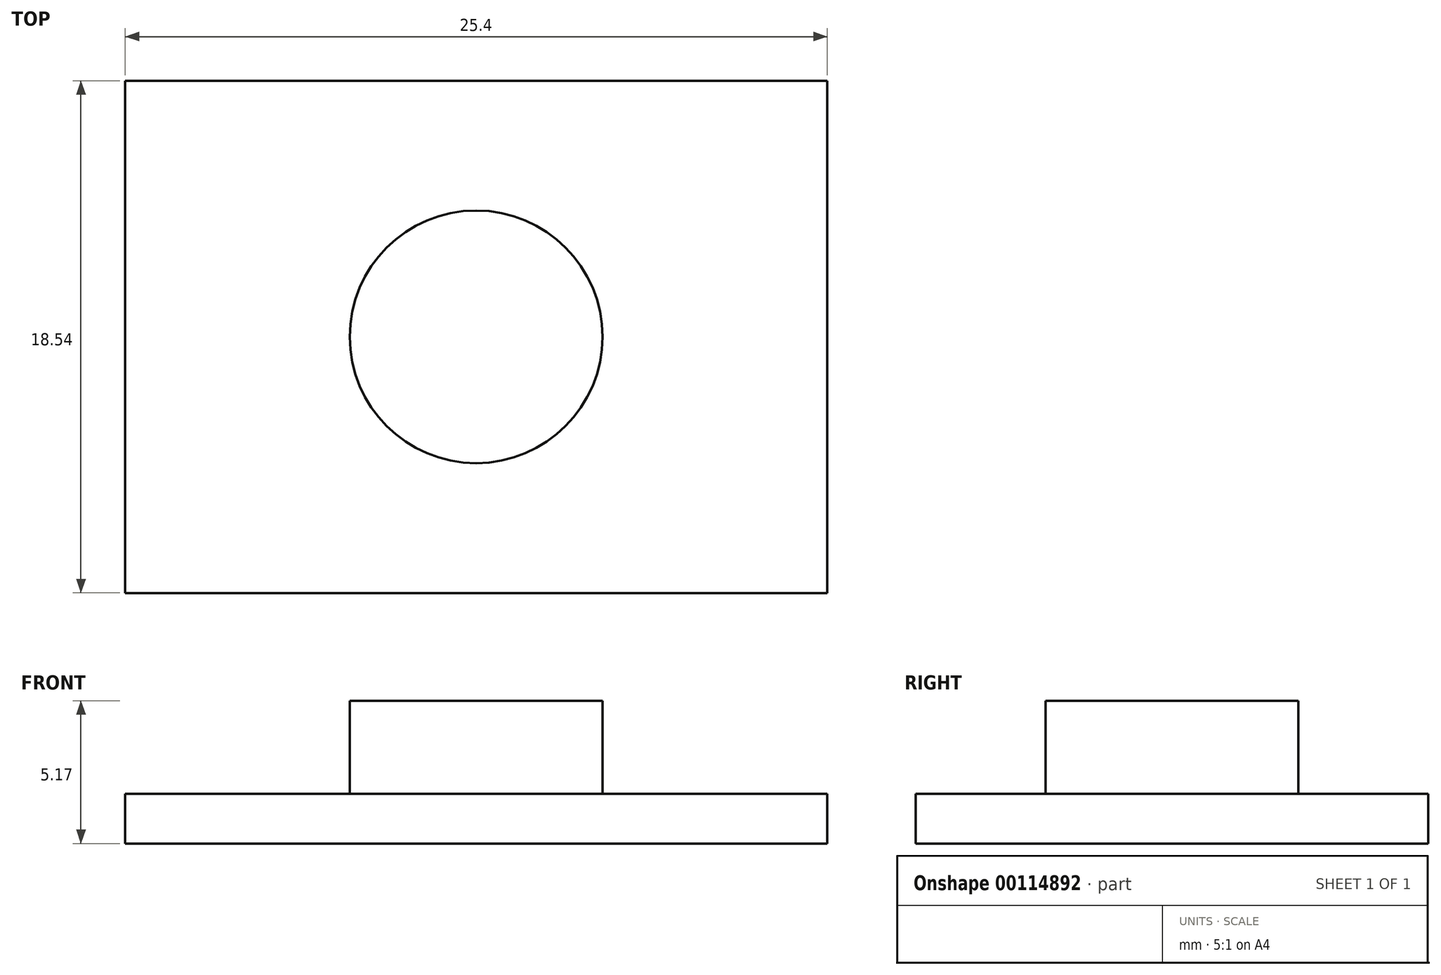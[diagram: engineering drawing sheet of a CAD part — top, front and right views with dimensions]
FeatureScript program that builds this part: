
annotation { "Feature Type Name" : "Feature", "Feature Type Description" : "" }
export const myFeature = defineFeature(function(context is Context, id is Id, definition is map)
    precondition{}
    {
        {
            var Q0;
            Q0=qCreatedBy(makeId("Top.planeOp"),FACE);
            var sketch = newSketch(context, id + "F0", { "sketchPlane" : qUnion([Q0])});
            skLineSegment(sketch, "E0.bottom", {"start": v(-54.14, 26.58) * mm, "end": v(-28.74, 26.58) * mm});
            skLineSegment(sketch, "E0.top", {"start": v(-54.14, 8.04) * mm, "end": v(-28.74, 8.04) * mm});
            skLineSegment(sketch, "E0.left", {"start": v(-54.14, 26.58) * mm, "end": v(-54.14, 8.04) * mm});
            skLineSegment(sketch, "E0.right", {"start": v(-28.74, 26.58) * mm, "end": v(-28.74, 8.04) * mm});
            skSolve(sketch);
        }
        {
            var Q0;
            Q0 = qSketchRegion(id + "F0", true);
            extrude(context, id + "F1", {"entities" : qUnion([Q0]), "depth" : 1.8 * mm});
        }
        {
            var Q0;
            Q0=makeQuery(id+"F1.opExtrude","CAP_FACE",FACE,{"disambiguationData":[OSD([sQuery(id+"F0.wireOp",EDGE,"E0.bottom"),sQuery(id+"F0.wireOp",EDGE,"E0.top"),sQuery(id+"F0.wireOp",EDGE,"E0.left"),sQuery(id+"F0.wireOp",EDGE,"E0.right")])],"isStart":false});
            var sketch = newSketch(context, id + "F2", { "sketchPlane" : qUnion([Q0])});
            skCircle(sketch, "E1", {"center": v(-41.45, 17.31) * mm, "radius": 4.57 * mm});
            skSolve(sketch);
        }
        {
            var Q0;
            Q0 = qSketchRegion(id + "F2", true);
            extrude(context, id + "F3", {"entities" : qUnion([Q0]), "operationType" : NewBodyOperationType.ADD, "endBound" : BoundingType.SYMMETRIC, "depth" : 6.73 * mm});
        }
        {
            var Q0;
            Q0=makeQuery(id+"F3.opExtrude","CAP_FACE",FACE,{"disambiguationData":[OSD([sQuery(id+"F2.wireOp",EDGE,"E1")])],"isStart":true});
            var Q1;
            Q1=makeQuery(id+"F1.opExtrude","CAP_FACE",FACE,{"disambiguationData":[OSD([sQuery(id+"F0.wireOp",EDGE,"E0.bottom"),sQuery(id+"F0.wireOp",EDGE,"E0.top"),sQuery(id+"F0.wireOp",EDGE,"E0.left"),sQuery(id+"F0.wireOp",EDGE,"E0.right")])],"isStart":true});
            extrude(context, id + "F4", {"entities" : qUnion([Q0]), "operationType" : NewBodyOperationType.REMOVE, "endBound" : BoundingType.UP_TO_SURFACE, "oppositeDirection" : true, "endBoundEntityFace" : qUnion([Q1]), "depth" : 25.4 * mm});
        }
    });
